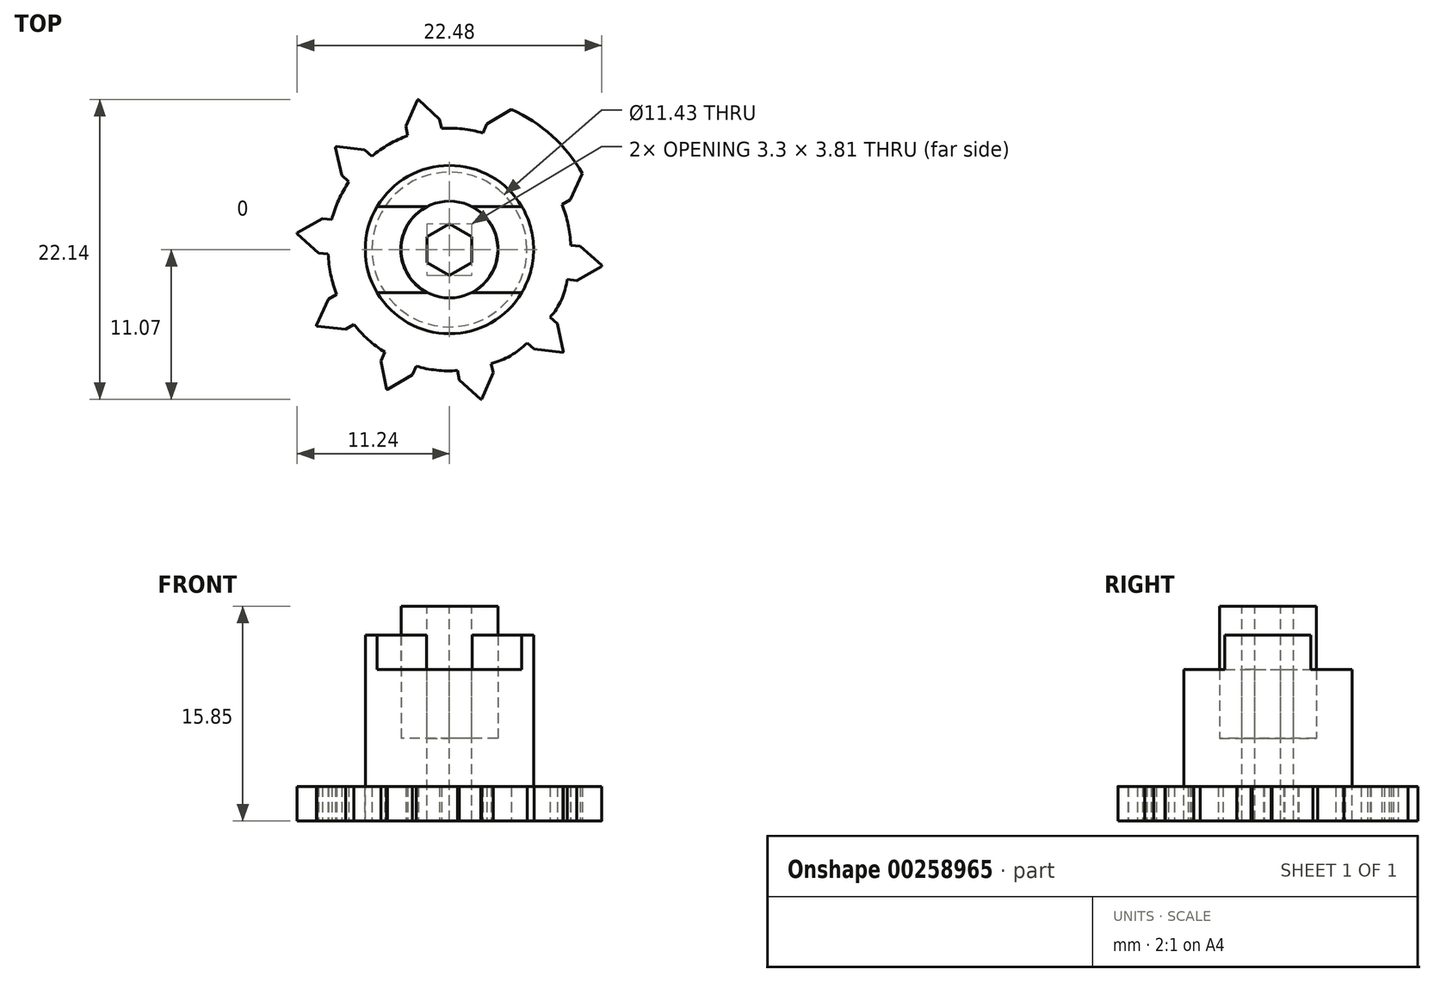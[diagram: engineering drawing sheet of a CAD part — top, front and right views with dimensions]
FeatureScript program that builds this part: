
annotation { "Feature Type Name" : "Feature", "Feature Type Description" : "" }
export const myFeature = defineFeature(function(context is Context, id is Id, definition is map)
    precondition{}
    {
        {
            var Q0;
            Q0=qCreatedBy(makeId("Top.planeOp"),FACE);
            var sketch = newSketch(context, id + "F0", { "sketchPlane" : qUnion([Q0])});
            skCircle(sketch, "E0", {"center": v(0, 0) * mm, "radius": 11.3 * mm});
            skCircle(sketch, "E1", {"center": v(0, 0) * mm, "radius": 5.72 * mm});
            skSolve(sketch);
        }
        {
            var Q0;
            Q0 = qSketchRegion(id + "F0", true);
            extrude(context, id + "F1", {"entities" : qUnion([Q0]), "depth" : 2.54 * mm});
        }
        {
            var Q0;
            Q0=makeQuery(id+"F1.opExtrude","CAP_FACE",FACE,{"disambiguationData":[OSD([sQuery(id+"F0.wireOp",EDGE,"E0"),sQuery(id+"F0.wireOp",EDGE,"E1")])],"isStart":false});
            var sketch = newSketch(context, id + "F2", { "sketchPlane" : qUnion([Q0])});
            skCircle(sketch, "E2", {"center": v(0, 0) * mm, "radius": 7.34 * mm});
            skSolve(sketch);
        }
        {
            var Q0;
            Q0=makeQuery(id+"F2.imprint","IMPRINT",FACE,{"disambiguationData":[TD([[makeQuery(id+"F2.imprint","IMPRINT",EDGE,{"derivedFrom":sQuery(id+"F2.wireOp",EDGE,"E2")}),-1.0]])]});
            cPlane(context, id + "F3", {"entities" : qUnion([Q0]), "cplaneType" : CPlaneType.OFFSET, "offset" : 8.64 * mm, "width" : 152.4 * mm, "height" : 152.4 * mm});
        }
        {
            var Q0;
            Q0=qCreatedBy(id+"F3.planeOp",FACE);
            var sketch = newSketch(context, id + "F4", { "sketchPlane" : qUnion([Q0])});
            skCircle(sketch, "E3", {"center": v(0, 0) * mm, "radius": 6.21 * mm});
            skSolve(sketch);
        }
        {
            var Q0;
            Q0=qCreatedBy(id+"F3.planeOp",FACE);
            var sketch = newSketch(context, id + "F5", { "sketchPlane" : qUnion([Q0])});
            skCircle(sketch, "E4", {"center": v(0, 0) * mm, "radius": 3.57 * mm});
            skSolve(sketch);
        }
        {
            var Q0;
            Q0 = qSketchRegion(id + "F5", true);
            extrude(context, id + "F6", {"entities" : qUnion([Q0]), "depth" : 4.67 * mm, "hasSecondDirection" : true, "secondDirectionOppositeDirection" : true, "secondDirectionDepth" : 5.08 * mm});
        }
        {
            var Q0;
            Q0=qCreatedBy(id+"F3.planeOp",FACE);
            var sketch = newSketch(context, id + "F7", { "sketchPlane" : qUnion([Q0])});
            skCircle(sketch, "E5.cCircle", {"center": v(0, 0) * mm, "radius": 1.37 * mm, "construction": true});
            skLineSegment(sketch, "E5.0", {"start": v(0.37, 1.54) * mm, "end": v(1.52, 0.45) * mm});
            skLineSegment(sketch, "E5.1", {"start": v(1.52, 0.45) * mm, "end": v(1.15, -1.09) * mm});
            skLineSegment(sketch, "E5.2", {"start": v(1.15, -1.09) * mm, "end": v(-0.37, -1.54) * mm});
            skLineSegment(sketch, "E5.3", {"start": v(-0.37, -1.54) * mm, "end": v(-1.52, -0.45) * mm});
            skLineSegment(sketch, "E5.4", {"start": v(-1.52, -0.45) * mm, "end": v(-1.15, 1.09) * mm});
            skLineSegment(sketch, "E5.5", {"start": v(-1.15, 1.09) * mm, "end": v(0.37, 1.54) * mm});
            skPoint(sketch, "E5.0.midPoint", {"position": v(0.94, 1) * mm});
            skSolve(sketch);
        }
        {
            var Q0;
            Q0 = qSketchRegion(id + "F7", true);
            extrude(context, id + "F8", {"entities" : qUnion([Q0]), "operationType" : NewBodyOperationType.REMOVE, "oppositeDirection" : true, "depth" : 50.8 * mm});
        }
        {
            var Q0;
            Q0=makeQuery(id+"F1.opExtrude","CAP_FACE",FACE,{"disambiguationData":[OSD([sQuery(id+"F0.wireOp",EDGE,"E0"),sQuery(id+"F0.wireOp",EDGE,"E1")])],"isStart":true});
            var sketch = newSketch(context, id + "F9", { "sketchPlane" : qUnion([Q0])});
            skPoint(sketch, "E6.0.midPoint", {"position": v(5.38, 9.36) * mm});
            skLineSegment(sketch, "E7.trimOffspring", {"start": v(-5.07, 8.22) * mm, "end": v(-4.78, 7.57) * mm});
            skLineSegment(sketch, "E8", {"start": v(-5.07, 8.22) * mm, "end": v(-4.63, 10.36) * mm});
            skLineSegment(sketch, "E9", {"start": v(-4.63, 10.36) * mm, "end": v(-2.75, 9.25) * mm});
            skLineSegment(sketch, "E10.trimOffspring", {"start": v(-2.75, 9.25) * mm, "end": v(-2.46, 8.6) * mm});
            skLineSegment(sketch, "E11.1.0", {"start": v(-8.93, 3.67) * mm, "end": v(-9.84, 5.66) * mm});
            skLineSegment(sketch, "E11.1.1", {"start": v(-9.84, 5.66) * mm, "end": v(-7.66, 5.87) * mm});
            skLineSegment(sketch, "E11.2.0", {"start": v(-9.38, -2.28) * mm, "end": v(-11.29, -1.2) * mm});
            skLineSegment(sketch, "E11.2.1", {"start": v(-11.29, -1.2) * mm, "end": v(-9.65, 0.25) * mm});
            skLineSegment(sketch, "E11.3.0", {"start": v(-6.25, -7.36) * mm, "end": v(-8.42, -7.6) * mm});
            skLineSegment(sketch, "E11.3.1", {"start": v(-8.42, -7.6) * mm, "end": v(-7.95, -5.47) * mm});
            skLineSegment(sketch, "E11.4.0", {"start": v(-0.73, -9.62) * mm, "end": v(-2.34, -11.1) * mm});
            skLineSegment(sketch, "E11.4.1", {"start": v(-2.34, -11.1) * mm, "end": v(-3.22, -9.1) * mm});
            skLineSegment(sketch, "E11.5.0", {"start": v(5.07, -8.22) * mm, "end": v(4.63, -10.36) * mm});
            skLineSegment(sketch, "E11.5.1", {"start": v(4.63, -10.36) * mm, "end": v(2.75, -9.25) * mm});
            skLineSegment(sketch, "E11.6.0", {"start": v(8.93, -3.67) * mm, "end": v(9.84, -5.66) * mm});
            skLineSegment(sketch, "E11.6.1", {"start": v(9.84, -5.66) * mm, "end": v(7.66, -5.87) * mm});
            skLineSegment(sketch, "E11.7.0", {"start": v(9.38, 2.28) * mm, "end": v(11.29, 1.2) * mm});
            skLineSegment(sketch, "E11.7.1", {"start": v(11.29, 1.2) * mm, "end": v(9.65, -0.25) * mm});
            skLineSegment(sketch, "E11.8.0", {"start": v(6.25, 7.36) * mm, "end": v(8.42, 7.6) * mm});
            skLineSegment(sketch, "E11.8.1", {"start": v(8.42, 7.6) * mm, "end": v(7.95, 5.47) * mm});
            skLineSegment(sketch, "E11.9.0", {"start": v(0.73, 9.62) * mm, "end": v(2.34, 11.1) * mm});
            skLineSegment(sketch, "E11.9.1", {"start": v(2.34, 11.1) * mm, "end": v(3.22, 9.1) * mm});
            skPoint(sketch, "E11.center", {"position": v(0, 0) * mm});
            skCircle(sketch, "E12", {"center": v(0, 0) * mm, "radius": 11.35 * mm});
            skPoint(sketch, "E13.orphan", {"position": v(-4.63, 10.36) * mm});
            skLineSegment(sketch, "E14.trimOffspring", {"start": v(4.78, -7.57) * mm, "end": v(5.07, -8.22) * mm});
            skLineSegment(sketch, "E15.1.1", {"start": v(-8.93, 3.67) * mm, "end": v(-8.32, 3.32) * mm});
            skLineSegment(sketch, "E15.1.2", {"start": v(-7.66, 5.87) * mm, "end": v(-7.05, 5.52) * mm});
            skLineSegment(sketch, "E15.2.1", {"start": v(-9.38, -2.28) * mm, "end": v(-8.68, -2.2) * mm});
            skLineSegment(sketch, "E15.2.2", {"start": v(-9.65, 0.25) * mm, "end": v(-8.95, 0.32) * mm});
            skLineSegment(sketch, "E15.3.1", {"start": v(-6.25, -7.36) * mm, "end": v(-5.73, -6.88) * mm});
            skLineSegment(sketch, "E15.3.2", {"start": v(-7.95, -5.47) * mm, "end": v(-7.43, -5) * mm});
            skLineSegment(sketch, "E15.4.1", {"start": v(-0.73, -9.62) * mm, "end": v(-0.59, -8.93) * mm});
            skLineSegment(sketch, "E15.4.2", {"start": v(-3.22, -9.1) * mm, "end": v(-3.07, -8.41) * mm});
            skLineSegment(sketch, "E15.5.1", {"start": v(5.07, -8.22) * mm, "end": v(4.78, -7.57) * mm});
            skLineSegment(sketch, "E15.5.2", {"start": v(2.75, -9.25) * mm, "end": v(2.46, -8.6) * mm});
            skLineSegment(sketch, "E15.6.1", {"start": v(8.93, -3.67) * mm, "end": v(8.32, -3.32) * mm});
            skLineSegment(sketch, "E15.6.2", {"start": v(7.66, -5.87) * mm, "end": v(7.05, -5.52) * mm});
            skLineSegment(sketch, "E15.7.1", {"start": v(9.38, 2.28) * mm, "end": v(8.68, 2.2) * mm});
            skLineSegment(sketch, "E15.7.2", {"start": v(9.65, -0.25) * mm, "end": v(8.95, -0.32) * mm});
            skLineSegment(sketch, "E15.8.1", {"start": v(6.25, 7.36) * mm, "end": v(5.73, 6.88) * mm});
            skLineSegment(sketch, "E15.8.2", {"start": v(7.95, 5.47) * mm, "end": v(7.43, 5) * mm});
            skLineSegment(sketch, "E15.9.1", {"start": v(0.73, 9.62) * mm, "end": v(0.59, 8.93) * mm});
            skLineSegment(sketch, "E15.9.2", {"start": v(3.22, 9.1) * mm, "end": v(3.07, 8.41) * mm});
            skArc(sketch, "E16", {"start": v(-8.32, 3.32) * mm, "mid": v(-8.76, 1.85) * mm, "end": v(-8.95, 0.32) * mm});
            skArc(sketch, "E17.trimOffspring", {"start": v(-8.68, -2.2) * mm, "mid": v(-8.17, -3.65) * mm, "end": v(-7.43, -5) * mm});
            skArc(sketch, "E18.trimOffspring", {"start": v(-5.73, -6.88) * mm, "mid": v(-4.46, -7.76) * mm, "end": v(-3.07, -8.41) * mm});
            skArc(sketch, "E19.trimOffspring", {"start": v(-0.59, -8.93) * mm, "mid": v(0.95, -8.9) * mm, "end": v(2.46, -8.6) * mm});
            skArc(sketch, "E20.trimOffspring", {"start": v(4.78, -7.57) * mm, "mid": v(6, -6.64) * mm, "end": v(7.05, -5.52) * mm});
            skArc(sketch, "E21.trimOffspring", {"start": v(8.32, -3.32) * mm, "mid": v(8.76, -1.85) * mm, "end": v(8.95, -0.32) * mm});
            skPoint(sketch, "E22.orphan", {"position": v(8.42, 7.6) * mm});
            skPoint(sketch, "E23.start.orphan", {"position": v(2.34, 11.1) * mm});
            skArc(sketch, "E24.trimOffspring", {"start": v(0.59, 8.93) * mm, "mid": v(-0.95, 8.9) * mm, "end": v(-2.46, 8.6) * mm});
            skArc(sketch, "E25.trimOffspring", {"start": v(-4.78, 7.57) * mm, "mid": v(-6, 6.64) * mm, "end": v(-7.05, 5.52) * mm});
            skArc(sketch, "E26", {"start": v(5.73, 6.88) * mm, "mid": v(4.5, 7.84) * mm, "end": v(3.07, 8.41) * mm});
            skArc(sketch, "E27", {"start": v(8.68, 2.2) * mm, "mid": v(8.27, 3.7) * mm, "end": v(7.43, 5) * mm});
            skSolve(sketch);
        }
        {
            var Q0;
            {var subQ4=sQuery(id+"F9.wireOp",EDGE,"E15.1.1");Q0=makeQuery(id+"F9.imprint","IMPRINT",FACE,{"disambiguationData":[TD([[makeQuery(id+"F9.imprint","IMPRINT",EDGE,{"derivedFrom":subQ4}),-1.0]])]});}
            var Q1;
            {var subQ5=sQuery(id+"F9.wireOp",EDGE,"E7.trimOffspring");Q1=makeQuery(id+"F9.imprint","IMPRINT",FACE,{"disambiguationData":[TD([[makeQuery(id+"F9.imprint","IMPRINT",EDGE,{"derivedFrom":subQ5}),-1.0]])]});}
            var Q2;
            {var subQ4=sQuery(id+"F9.wireOp",EDGE,"E10.trimOffspring");Q2=makeQuery(id+"F9.imprint","IMPRINT",FACE,{"disambiguationData":[TD([[makeQuery(id+"F9.imprint","IMPRINT",EDGE,{"derivedFrom":subQ4}),1.0]])]});}
            var Q3;
            {var subQ1=sQuery(id+"F9.wireOp",EDGE,"E15.8.1");Q3=makeQuery(id+"F9.imprint","IMPRINT",FACE,{"disambiguationData":[TD([[makeQuery(id+"F9.imprint","IMPRINT",EDGE,{"derivedFrom":subQ1}),-1.0]])]});}
            var Q4;
            {var subQ0=sQuery(id+"F9.wireOp",EDGE,"E15.7.1");Q4=makeQuery(id+"F9.imprint","IMPRINT",FACE,{"disambiguationData":[TD([[makeQuery(id+"F9.imprint","IMPRINT",EDGE,{"derivedFrom":subQ0}),-1.0]])]});}
            var Q5;
            {var subQ1=sQuery(id+"F9.wireOp",EDGE,"E15.6.1");Q5=makeQuery(id+"F9.imprint","IMPRINT",FACE,{"disambiguationData":[TD([[makeQuery(id+"F9.imprint","IMPRINT",EDGE,{"derivedFrom":subQ1}),-1.0]])]});}
            var Q6;
            {var subQ4=sQuery(id+"F9.wireOp",EDGE,"E15.5.1");Q6=makeQuery(id+"F9.imprint","IMPRINT",FACE,{"disambiguationData":[TD([[makeQuery(id+"F9.imprint","IMPRINT",EDGE,{"derivedFrom":subQ4}),-1.0]])]});}
            var Q7;
            {var subQ1=sQuery(id+"F9.wireOp",EDGE,"E15.4.1");Q7=makeQuery(id+"F9.imprint","IMPRINT",FACE,{"disambiguationData":[TD([[makeQuery(id+"F9.imprint","IMPRINT",EDGE,{"derivedFrom":subQ1}),-1.0]])]});}
            var Q8;
            {var subQ0=sQuery(id+"F9.wireOp",EDGE,"E15.3.1");Q8=makeQuery(id+"F9.imprint","IMPRINT",FACE,{"disambiguationData":[TD([[makeQuery(id+"F9.imprint","IMPRINT",EDGE,{"derivedFrom":subQ0}),-1.0]])]});}
            var Q9;
            {var subQ1=sQuery(id+"F9.wireOp",EDGE,"E15.2.1");Q9=makeQuery(id+"F9.imprint","IMPRINT",FACE,{"disambiguationData":[TD([[makeQuery(id+"F9.imprint","IMPRINT",EDGE,{"derivedFrom":subQ1}),-1.0]])]});}
            extrude(context, id + "F10", {"entities" : qUnion([Q0, Q1, Q2, Q3, Q4, Q5, Q6, Q7, Q8, Q9]), "operationType" : NewBodyOperationType.REMOVE, "oppositeDirection" : true, "depth" : 25.4 * mm});
        }
        {
            var Q0;
            Q0=qCreatedBy(makeId("Right.planeOp"),FACE);
            var sketch = newSketch(context, id + "F11", { "sketchPlane" : qUnion([Q0])});
            skLineSegment(sketch, "E28", {"start": v(0, 0) * mm, "end": v(0, 11.2) * mm});
            skLineSegment(sketch, "E29", {"start": v(-6.18, 11.18) * mm, "end": v(-7.32, 2.54) * mm});
            skLineSegment(sketch, "E30", {"start": v(-6.18, 11.18) * mm, "end": v(0, 11.2) * mm});
            skLineSegment(sketch, "E31", {"start": v(-7.32, 2.54) * mm, "end": v(0, 2.56) * mm});
            skSolve(sketch);
        }
        {
            var Q0;
            Q0=makeQuery(id+"F6.opExtrude","CAP_FACE",FACE,{"disambiguationData":[OSD([sQuery(id+"F5.wireOp",EDGE,"E4")])],"isStart":false});
            var sketch = newSketch(context, id + "F12", { "sketchPlane" : qUnion([Q0])});
            skCircle(sketch, "E32.cCircle", {"center": v(0, 0) * mm, "radius": 1.65 * mm, "construction": true});
            skLineSegment(sketch, "E32.0", {"start": v(-1.65, 0.95) * mm, "end": v(0, 1.9) * mm});
            skLineSegment(sketch, "E32.1", {"start": v(0, 1.9) * mm, "end": v(1.65, 0.95) * mm});
            skLineSegment(sketch, "E32.2", {"start": v(1.65, 0.95) * mm, "end": v(1.65, -0.95) * mm});
            skLineSegment(sketch, "E32.3", {"start": v(1.65, -0.95) * mm, "end": v(0, -1.9) * mm});
            skLineSegment(sketch, "E32.4", {"start": v(0, -1.9) * mm, "end": v(-1.65, -0.95) * mm});
            skLineSegment(sketch, "E32.5", {"start": v(-1.65, -0.95) * mm, "end": v(-1.65, 0.95) * mm});
            skPoint(sketch, "E32.0.midPoint", {"position": v(-0.83, 1.43) * mm});
            skSolve(sketch);
        }
        {
            var Q0;
            Q0 = qSketchRegion(id + "F12", true);
            var Q1;
            Q1=makeQuery(id+"F1.opExtrude","CAP_FACE",FACE,{"disambiguationData":[OSD([sQuery(id+"F0.wireOp",EDGE,"E0"),sQuery(id+"F0.wireOp",EDGE,"E1")])],"isStart":true});
            var Q2;
            Q2=makeQuery(id+"F6.opExtrude","CAP_FACE",FACE,{"disambiguationData":[OSD([sQuery(id+"F5.wireOp",EDGE,"E4")])],"isStart":false});
            extrude(context, id + "F13", {"entities" : qUnion([Q0]), "operationType" : NewBodyOperationType.REMOVE, "oppositeDirection" : true, "endBoundEntityFace" : qUnion([Q1]), "depth" : 25.4 * mm});
        }
        {
            var Q0;
            Q0=makeQuery(id+"F2.imprint","IMPRINT",FACE,{"disambiguationData":[TD([[makeQuery(id+"F2.imprint","IMPRINT",EDGE,{"derivedFrom":makeQuery(id+"F1.opExtrude","CAP_EDGE",EDGE,{"disambiguationData":[OSD([sQuery(id+"F0.wireOp",EDGE,"E1")])],"isStart":false})}),1.0]])]});
            var sketch = newSketch(context, id + "F14", { "sketchPlane" : qUnion([Q0])});
            skCircle(sketch, "E33.cCircle", {"center": v(0, 0) * mm, "radius": 1.65 * mm, "construction": true});
            skLineSegment(sketch, "E33.0", {"start": v(-1.65, 0.95) * mm, "end": v(0, 1.9) * mm});
            skLineSegment(sketch, "E33.1", {"start": v(0, 1.9) * mm, "end": v(1.65, 0.95) * mm});
            skLineSegment(sketch, "E33.2", {"start": v(1.65, 0.95) * mm, "end": v(1.65, -0.95) * mm});
            skLineSegment(sketch, "E33.3", {"start": v(1.65, -0.95) * mm, "end": v(0, -1.9) * mm});
            skLineSegment(sketch, "E33.4", {"start": v(0, -1.9) * mm, "end": v(-1.65, -0.95) * mm});
            skLineSegment(sketch, "E33.5", {"start": v(-1.65, -0.95) * mm, "end": v(-1.65, 0.95) * mm});
            skPoint(sketch, "E33.0.midPoint", {"position": v(-0.83, 1.43) * mm});
            skSolve(sketch);
        }
        {
            var Q0;
            Q0 = qSketchRegion(id + "F4", true);
            var Q1;
            Q1=makeQuery(id+"F1.opExtrude","CAP_FACE",FACE,{"disambiguationData":[OSD([sQuery(id+"F0.wireOp",EDGE,"E0"),sQuery(id+"F0.wireOp",EDGE,"E1")])],"isStart":true});
            extrude(context, id + "F15", {"entities" : qUnion([Q0]), "endBound" : BoundingType.UP_TO_SURFACE, "oppositeDirection" : true, "endBoundEntityFace" : qUnion([Q1]), "depth" : 25.4 * mm});
        }
        {
            var Q0;
            Q0 = qSketchRegion(id + "F14", true);
            extrude(context, id + "F16", {"entities" : qUnion([Q0]), "operationType" : NewBodyOperationType.REMOVE, "oppositeDirection" : true, "depth" : 50.8 * mm, "hasSecondDirection" : true, "secondDirectionOppositeDirection" : false, "secondDirectionDepth" : 50.8 * mm});
        }
        {
            var Q0;
            Q0=makeQuery(id+"F15.opExtrude","CAP_FACE",FACE,{"disambiguationData":[OSD([sQuery(id+"F4.wireOp",EDGE,"E3")])],"isStart":true});
            var sketch = newSketch(context, id + "F17", { "sketchPlane" : qUnion([Q0])});
            skArc(sketch, "E34", {"start": v(-1.9, -3.04) * mm, "mid": v(-1.8, -3.11) * mm, "end": v(-1.68, -3.18) * mm});
            skArc(sketch, "E35.trimOffspring", {"start": v(3.4, 1.18) * mm, "mid": v(2.72, 2.34) * mm, "end": v(1.68, 3.17) * mm});
            skPoint(sketch, "E36.start.orphan", {"position": v(0, 6.21) * mm});
            skArc(sketch, "E37", {"start": v(-1.68, 3.17) * mm, "mid": v(-3.6, 0) * mm, "end": v(-1.68, -3.18) * mm});
            skArc(sketch, "E38.MirrorC", {"start": v(-1.68, -3.18) * mm, "mid": v(-3.6, 0) * mm, "end": v(-1.68, 3.17) * mm});
            skLineSegment(sketch, "E39.bottom", {"start": v(-5.34, -3.18) * mm, "end": v(-1.68, -3.18) * mm});
            skLineSegment(sketch, "E39.top", {"start": v(-5.34, 3.18) * mm, "end": v(-1.68, 3.18) * mm});
            skPoint(sketch, "E40.orphan", {"position": v(-6.54, -3.18) * mm});
            skPoint(sketch, "E41.orphan", {"position": v(6.21, 0) * mm});
            skArc(sketch, "E42.trimOffspring", {"start": v(-1.68, 3.18) * mm, "mid": v(-1.8, 3.11) * mm, "end": v(-1.9, 3.04) * mm});
            skArc(sketch, "E43.trimOffspring", {"start": v(1.68, 3.17) * mm, "mid": v(3.34, 1.31) * mm, "end": v(3.4, -1.18) * mm});
            skLineSegment(sketch, "E44.trimOffspring", {"start": v(1.68, 3.18) * mm, "end": v(5.34, 3.18) * mm});
            skArc(sketch, "E45.trimOffspring", {"start": v(1.68, -3.17) * mm, "mid": v(3.6, 0) * mm, "end": v(1.68, 3.17) * mm});
            skLineSegment(sketch, "E46.trimOffspring", {"start": v(1.68, -3.18) * mm, "end": v(5.34, -3.18) * mm});
            skPoint(sketch, "E47.trimOffspring.end.orphan", {"position": v(6.21, 3.18) * mm});
            skPoint(sketch, "E48.start.orphan", {"position": v(-6.54, 0) * mm});
            skArc(sketch, "E49", {"start": v(-5.34, 3.17) * mm, "mid": v(-6.21, 0) * mm, "end": v(-5.34, -3.18) * mm});
            skArc(sketch, "E50.trimOffspring", {"start": v(5.34, -3.18) * mm, "mid": v(6.21, 0) * mm, "end": v(5.34, 3.17) * mm});
            skSolve(sketch);
        }
        {
            var Q0;
            Q0 = qSketchRegion(id + "F17", true);
            extrude(context, id + "F18", {"entities" : qUnion([Q0]), "operationType" : NewBodyOperationType.ADD, "depth" : 2.54 * mm});
        }
    });
